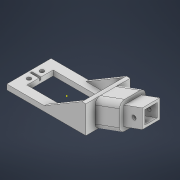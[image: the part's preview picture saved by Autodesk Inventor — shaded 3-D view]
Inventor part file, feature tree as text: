
AUTODESK INVENTOR PART (.ipt)
format: ipt  version: 2021 (Build 250183000, 183)  size: 417,792 bytes
history: native  units: mm
features: extrude x11, sketch x8, other x1, shell x1, fillet x1
ambient origin geometry x8: Origin, YZ Plane, XZ Plane, XY Plane, X Axis, Y Axis, Z Axis, Center Point
bodies: Body1 (feature_tree)
feature tree (22):
  other  "Servohalterung_v2"
  extrude  "Extrusion2"  Depth=20.2mm
  extrude  "Extrusion3"  Depth=7.0mm
  sketch  "Skizze3"  dims[d9=4.0mm d10=0.0mm d11=3.2mm]
  extrude  "Extrusion4"  Depth=4.0mm
  extrude  "Extrusion5"  Depth=10.0mm
  extrude  "Extrusion6"  Depth=4.0mm TaperAngle=0.0deg
  sketch  "Skizze6"  dims[d12=3.2mm d15=10.0mm]
  extrude  "Extrusion7"  Depth=1.5mm
  extrude  "Extrusion9"  Depth=7.0mm
  shell  "Wandung2"  Thickness=2.0mm
  fillet  "Rundung1"  Radius=3.0mm
  extrude  "Extrusion10"  Depth=20.0mm
  extrude  "Extrusion11"  Depth=21.216mm
  extrude  "Extrusion12"  Depth=10.0mm
  extrude  "Extrusion13"  Depth=34.2mm TaperAngle=0.0deg
  sketch  "Skizze1"  dims[d0=41.0mm d3=20.2mm]
  sketch  "Skizze2"  dims[d7=58.0mm d8=7.0mm]
  sketch  "Skizze7"  dims[d16=5.0mm d17=4.0mm d18=0.0mm]
  sketch  "Skizze8"  dims[d19=7.0mm d20=1.5mm]
  sketch  "Skizze9"  dims[d21=2.0mm d22=0.0mm d23=7.0mm d24=2.0mm d25=0.0mm d26=3.0mm]
  sketch  "Skizze10"  dims[d27=21.216mm d28=20.0mm d29=21.216mm d30=3.490659mm d31=34.2mm d32=0.0mm d33=20.0mm d34=0.0mm d36=4.0mm d38=19.198622mm d42=18.0mm d44=19.198622mm d48=14.314467mm d51=13.5mm d52=0.0mm d53=2.0mm d54=2.0mm d55=0.0mm d56=2.0mm d57=0.0mm d58=3.5mm d59=3.5mm d60=3.2mm d62=27.925268mm d63=8.0mm d64=10.0mm d65=0.0mm d66=14.5mm d67=27.925268mm d68=50.0mm d69=0.0mm]
